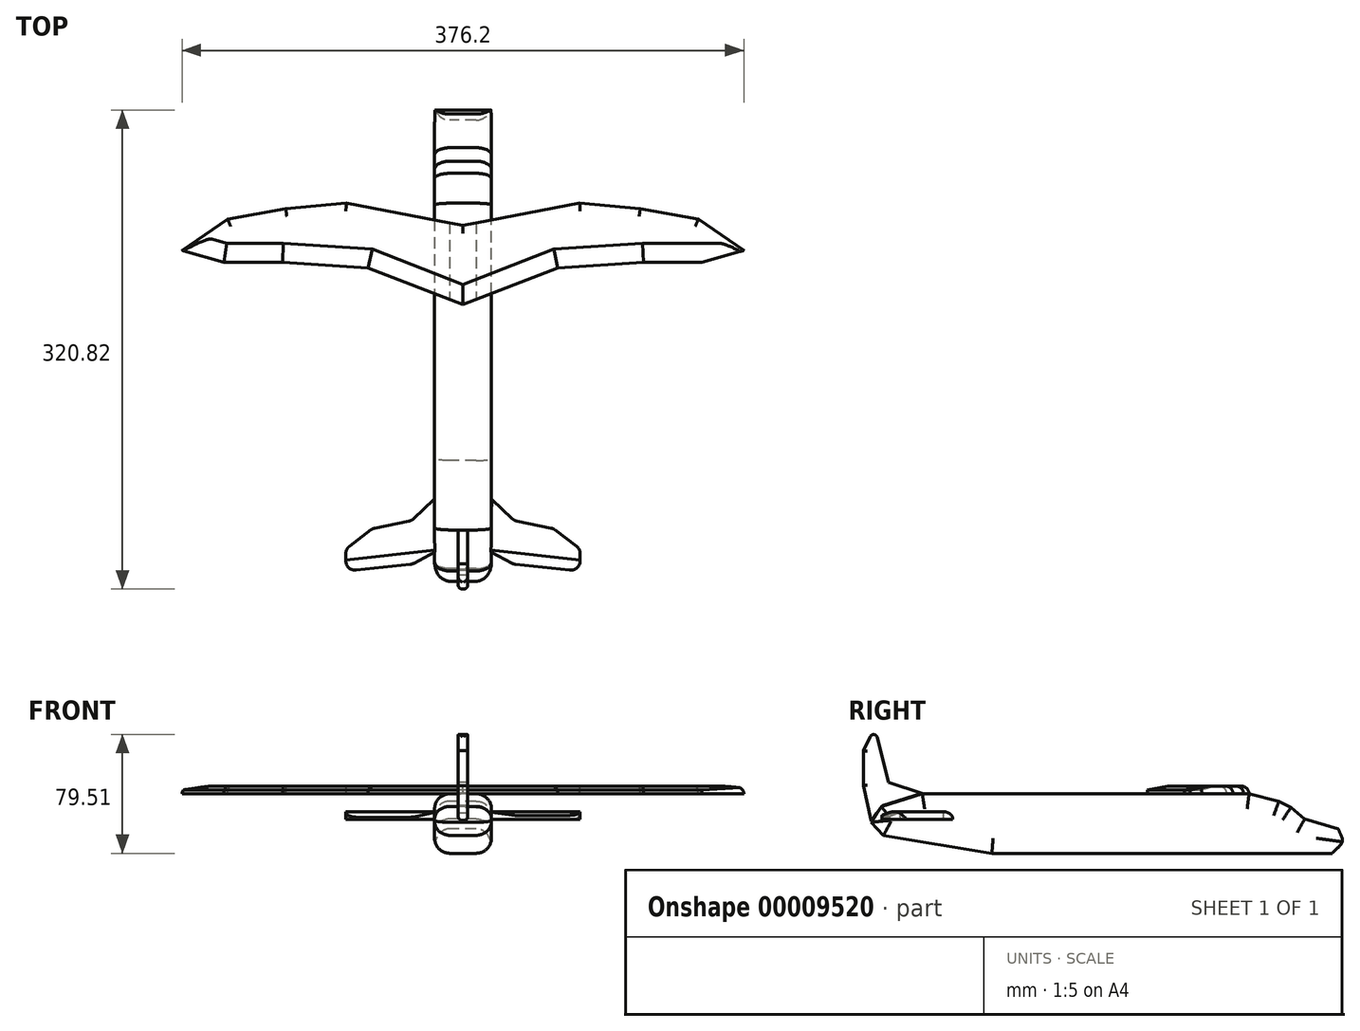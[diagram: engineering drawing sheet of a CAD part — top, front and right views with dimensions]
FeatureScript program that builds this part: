
annotation { "Feature Type Name" : "Feature", "Feature Type Description" : "" }
export const myFeature = defineFeature(function(context is Context, id is Id, definition is map)
    precondition{}
    {
        {
            var Q0;
            Q0=qCreatedBy(makeId("Right.planeOp"),FACE);
            var sketch = newSketch(context, id + "F0", { "sketchPlane" : qUnion([Q0])});
            skLineSegment(sketch, "E0", {"start": v(-78.46, 0) * mm, "end": v(149.41, 0) * mm});
            skLineSegment(sketch, "E1", {"start": v(149.41, 0) * mm, "end": v(157.23, 7.66) * mm});
            skLineSegment(sketch, "E2", {"start": v(157.23, 7.66) * mm, "end": v(153.48, 16.41) * mm});
            skLineSegment(sketch, "E3", {"start": v(153.48, 16.41) * mm, "end": v(130.97, 22.97) * mm});
            skLineSegment(sketch, "E4", {"start": v(130.97, 22.97) * mm, "end": v(121.9, 30.79) * mm});
            skLineSegment(sketch, "E5", {"start": v(121.9, 30.79) * mm, "end": v(113.78, 34.85) * mm});
            skLineSegment(sketch, "E6", {"start": v(113.78, 34.85) * mm, "end": v(93.77, 39.85) * mm});
            skLineSegment(sketch, "E7", {"start": v(93.77, 39.85) * mm, "end": v(-34.7, 39.85) * mm});
            skLineSegment(sketch, "E8", {"start": v(-34.7, 39.85) * mm, "end": v(-125.03, 39.85) * mm});
            skLineSegment(sketch, "E9", {"start": v(-125.03, 39.85) * mm, "end": v(-152.54, 31.41) * mm});
            skLineSegment(sketch, "E10", {"start": v(-152.54, 31.41) * mm, "end": v(-159.42, 20.79) * mm});
            skLineSegment(sketch, "E11", {"start": v(-159.42, 20.79) * mm, "end": v(-150.98, 12.03) * mm});
            skLineSegment(sketch, "E12", {"start": v(-150.98, 12.03) * mm, "end": v(-78.46, 0) * mm});
            skSolve(sketch);
        }
        {
            var Q0;
            Q0 = qSketchRegion(id + "F0", true);
            extrude(context, id + "F1", {"entities" : qUnion([Q0]), "endBound" : BoundingType.SYMMETRIC, "depth" : 38.1 * mm});
        }
        {
            var Q0;
            Q0=makeQuery(id+"F1.opExtrude","CAP_FACE",FACE,{"disambiguationData":[OSD([sQuery(id+"F0.wireOp",EDGE,"E0"),sQuery(id+"F0.wireOp",EDGE,"E1"),sQuery(id+"F0.wireOp",EDGE,"E2"),sQuery(id+"F0.wireOp",EDGE,"E3"),sQuery(id+"F0.wireOp",EDGE,"E4"),sQuery(id+"F0.wireOp",EDGE,"E5"),sQuery(id+"F0.wireOp",EDGE,"E6"),sQuery(id+"F0.wireOp",EDGE,"E7"),sQuery(id+"F0.wireOp",EDGE,"E8"),sQuery(id+"F0.wireOp",EDGE,"E9"),sQuery(id+"F0.wireOp",EDGE,"E10"),sQuery(id+"F0.wireOp",EDGE,"E11"),sQuery(id+"F0.wireOp",EDGE,"E12")])],"isStart":false});
            var Q1;
            Q1=makeQuery(id+"F1.opExtrude","CAP_FACE",FACE,{"disambiguationData":[OSD([sQuery(id+"F0.wireOp",EDGE,"E0"),sQuery(id+"F0.wireOp",EDGE,"E1"),sQuery(id+"F0.wireOp",EDGE,"E2"),sQuery(id+"F0.wireOp",EDGE,"E3"),sQuery(id+"F0.wireOp",EDGE,"E4"),sQuery(id+"F0.wireOp",EDGE,"E5"),sQuery(id+"F0.wireOp",EDGE,"E6"),sQuery(id+"F0.wireOp",EDGE,"E7"),sQuery(id+"F0.wireOp",EDGE,"E8"),sQuery(id+"F0.wireOp",EDGE,"E9"),sQuery(id+"F0.wireOp",EDGE,"E10"),sQuery(id+"F0.wireOp",EDGE,"E11"),sQuery(id+"F0.wireOp",EDGE,"E12")])],"isStart":true});
            fillet(context, id + "F2", {"entities" : qUnion([Q0, Q1]), "radius" : 10.16 * mm, "tangentPropagation" : true, "allowEdgeOverflow" : false});
        }
        {
            var Q0;
            Q0=makeQuery(id+"F1.opExtrude","SWEPT_EDGE",EDGE,{"disambiguationData":[OSD([sQuery(id+"F0.wireOp",EDGE,"E1"),sQuery(id+"F0.wireOp",EDGE,"E2")])]});
            fillet(context, id + "F3", {"entities" : qUnion([Q0]), "radius" : 5.08 * mm, "tangentPropagation" : true, "allowEdgeOverflow" : false});
        }
        {
            var Q0;
            Q0=makeQuery(id+"F1.opExtrude","SWEPT_FACE",FACE,{"disambiguationData":[OSD([sQuery(id+"F0.wireOp",EDGE,"E7"),sQuery(id+"F0.wireOp",EDGE,"E8")])]});
            var sketch = newSketch(context, id + "F4", { "sketchPlane" : qUnion([Q0])});
            skLineSegment(sketch, "E13", {"start": v(0, 78.89) * mm, "end": v(-78.16, 93.77) * mm});
            skLineSegment(sketch, "E14", {"start": v(-78.16, 93.77) * mm, "end": v(-118.71, 90.18) * mm});
            skLineSegment(sketch, "E15", {"start": v(-118.71, 90.18) * mm, "end": v(-157.58, 83.07) * mm});
            skLineSegment(sketch, "E16", {"start": v(-157.58, 83.07) * mm, "end": v(-188.1, 62.17) * mm});
            skLineSegment(sketch, "E17", {"start": v(-188.1, 62.17) * mm, "end": v(-160.1, 54.23) * mm});
            skLineSegment(sketch, "E18", {"start": v(-160.1, 54.23) * mm, "end": v(-120.8, 54.23) * mm});
            skLineSegment(sketch, "E19", {"start": v(-120.8, 54.23) * mm, "end": v(-63.54, 50.47) * mm});
            skLineSegment(sketch, "E20", {"start": v(-63.54, 50.47) * mm, "end": v(0, 25.8) * mm});
            skLineSegment(sketch, "E21", {"start": v(0, 0) * mm, "end": v(0, 154.96) * mm, "construction": true});
            skLineSegment(sketch, "E22.0.MirrorCS", {"start": v(78.16, 93.77) * mm, "end": v(118.71, 90.18) * mm});
            skLineSegment(sketch, "E22.1.MirrorCS", {"start": v(118.71, 90.18) * mm, "end": v(157.58, 83.07) * mm});
            skLineSegment(sketch, "E22.2.MirrorCS", {"start": v(63.54, 50.47) * mm, "end": v(0, 25.8) * mm});
            skLineSegment(sketch, "E22.3.MirrorCS", {"start": v(157.58, 83.07) * mm, "end": v(188.1, 62.17) * mm});
            skLineSegment(sketch, "E22.4.MirrorCS", {"start": v(188.1, 62.17) * mm, "end": v(160.1, 54.23) * mm});
            skLineSegment(sketch, "E22.5.MirrorCS", {"start": v(160.1, 54.23) * mm, "end": v(120.8, 54.23) * mm});
            skLineSegment(sketch, "E22.6.MirrorCS", {"start": v(0, 78.89) * mm, "end": v(78.16, 93.77) * mm});
            skLineSegment(sketch, "E22.7.MirrorCS", {"start": v(120.8, 54.23) * mm, "end": v(63.54, 50.47) * mm});
            skSolve(sketch);
        }
        {
            var Q0;
            Q0 = qSketchRegion(id + "F4", true);
            extrude(context, id + "F5", {"entities" : qUnion([Q0]), "operationType" : NewBodyOperationType.ADD, "depth" : 5.08 * mm});
        }
        {
            var Q0;
            Q0=qCreatedBy(makeId("Right.planeOp"),FACE);
            var sketch = newSketch(context, id + "F6", { "sketchPlane" : qUnion([Q0])});
            skLineSegment(sketch, "E23", {"start": v(-159.33, 21.94) * mm, "end": v(-164.55, 45.27) * mm});
            skLineSegment(sketch, "E24", {"start": v(-164.55, 45.27) * mm, "end": v(-164.55, 68.9) * mm});
            skLineSegment(sketch, "E25", {"start": v(-164.55, 68.9) * mm, "end": v(-156.87, 84.25) * mm});
            skLineSegment(sketch, "E26", {"start": v(-156.87, 84.25) * mm, "end": v(-147.67, 47.42) * mm});
            skLineSegment(sketch, "E27", {"start": v(-147.67, 47.42) * mm, "end": v(-125.26, 40.05) * mm});
            skLineSegment(sketch, "E28", {"start": v(-125.26, 40.05) * mm, "end": v(-151.66, 31.77) * mm});
            skLineSegment(sketch, "E29", {"start": v(-151.66, 31.77) * mm, "end": v(-159.33, 21.94) * mm});
            skSolve(sketch);
        }
        {
            var Q0;
            Q0=makeQuery(id+"F6.imprint","IMPRINT",FACE,{"disambiguationData":[TD([[makeQuery(id+"F6.imprint","IMPRINT",EDGE,{"derivedFrom":sQuery(id+"F6.wireOp",EDGE,"E23")}),-1.0]])]});
            extrude(context, id + "F7", {"entities" : qUnion([Q0]), "operationType" : NewBodyOperationType.ADD, "endBound" : BoundingType.SYMMETRIC, "depth" : 6.35 * mm});
        }
        {
            var Q0;
            Q0=makeQuery(id+"F7.opExtrude","CAP_EDGE",EDGE,{"disambiguationData":[OSD([sQuery(id+"F6.wireOp",EDGE,"E25")])],"isStart":false});
            var Q1;
            Q1=makeQuery(id+"F7.opExtrude","CAP_EDGE",EDGE,{"disambiguationData":[OSD([sQuery(id+"F6.wireOp",EDGE,"E24")])],"isStart":false});
            var Q2;
            Q2=makeQuery(id+"F7.opExtrude","CAP_EDGE",EDGE,{"disambiguationData":[OSD([sQuery(id+"F6.wireOp",EDGE,"E23")])],"isStart":false});
            var Q3;
            Q3=makeQuery(id+"F7.opExtrude","CAP_EDGE",EDGE,{"disambiguationData":[OSD([sQuery(id+"F6.wireOp",EDGE,"E23")])],"isStart":true});
            var Q4;
            Q4=makeQuery(id+"F7.opExtrude","CAP_EDGE",EDGE,{"disambiguationData":[OSD([sQuery(id+"F6.wireOp",EDGE,"E24")])],"isStart":true});
            var Q5;
            Q5=makeQuery(id+"F7.opExtrude","CAP_EDGE",EDGE,{"disambiguationData":[OSD([sQuery(id+"F6.wireOp",EDGE,"E25")])],"isStart":true});
            var Q6;
            Q6=makeQuery(id+"F7.opExtrude","SWEPT_EDGE",EDGE,{"disambiguationData":[OSD([sQuery(id+"F6.wireOp",EDGE,"E25"),sQuery(id+"F6.wireOp",EDGE,"E26")])]});
            fillet(context, id + "F8", {"entities" : qUnion([Q0, Q1, Q2, Q3, Q4, Q5, Q6]), "radius" : 2.54 * mm, "tangentPropagation" : true, "allowEdgeOverflow" : false});
        }
        {
            var Q0;
            Q0=qCreatedBy(makeId("Top.planeOp"),FACE);
            cPlane(context, id + "F9", {"entities" : qUnion([Q0]), "cplaneType" : CPlaneType.OFFSET, "offset" : 25.4 * mm, "width" : 152.4 * mm, "height" : 152.4 * mm});
        }
        {
            var Q0;
            Q0=qCreatedBy(id+"F9.planeOp",FACE);
            var sketch = newSketch(context, id + "F10", { "sketchPlane" : qUnion([Q0])});
            skLineSegment(sketch, "E30", {"start": v(19.38, -104.66) * mm, "end": v(33.06, -117.54) * mm});
            skLineSegment(sketch, "E31", {"start": v(36.15, -119.14) * mm, "end": v(58.99, -123.79) * mm});
            skLineSegment(sketch, "E32", {"start": v(61.55, -124.94) * mm, "end": v(75.97, -135.84) * mm});
            skLineSegment(sketch, "E33", {"start": v(78.49, -140.9) * mm, "end": v(78.49, -145.67) * mm});
            skLineSegment(sketch, "E34", {"start": v(71.45, -151.98) * mm, "end": v(35.17, -148.03) * mm});
            skLineSegment(sketch, "E35", {"start": v(32.84, -147.3) * mm, "end": v(17.61, -139.07) * mm});
            skLineSegment(sketch, "E36", {"start": v(19.38, -104.66) * mm, "end": v(17.61, -139.07) * mm});
            skPoint(sketch, "E37.visualSharp", {"position": v(78.49, -137.75) * mm});
            skArc(sketch, "E37.filletArc", {"start": v(78.49, -140.9) * mm, "mid": v(77.82, -138.08) * mm, "end": v(75.97, -135.84) * mm});
            skPoint(sketch, "E38.visualSharp", {"position": v(78.49, -152.74) * mm});
            skArc(sketch, "E38.filletArc", {"start": v(71.45, -151.98) * mm, "mid": v(76.38, -150.4) * mm, "end": v(78.49, -145.67) * mm});
            skPoint(sketch, "E39.visualSharp", {"position": v(60.4, -124.07) * mm});
            skArc(sketch, "E39.filletArc", {"start": v(61.55, -124.94) * mm, "mid": v(60.33, -124.22) * mm, "end": v(58.99, -123.79) * mm});
            skPoint(sketch, "E40.visualSharp", {"position": v(34.38, -118.78) * mm});
            skArc(sketch, "E40.filletArc", {"start": v(33.06, -117.54) * mm, "mid": v(34.5, -118.56) * mm, "end": v(36.15, -119.14) * mm});
            skPoint(sketch, "E41.visualSharp", {"position": v(33.93, -147.9) * mm});
            skArc(sketch, "E41.filletArc", {"start": v(32.84, -147.3) * mm, "mid": v(33.97, -147.78) * mm, "end": v(35.17, -148.03) * mm});
            skLineSegment(sketch, "E42", {"start": v(0, 0) * mm, "end": v(0, -233.9) * mm, "construction": true});
            skLineSegment(sketch, "E43.0.MirrorCS", {"start": v(-71.45, -151.98) * mm, "end": v(-35.17, -148.03) * mm});
            skLineSegment(sketch, "E44.0.MirrorCS", {"start": v(-78.49, -140.9) * mm, "end": v(-78.49, -145.67) * mm});
            skArc(sketch, "E44.1.MirrorCS", {"start": v(-78.49, -140.9) * mm, "mid": v(-77.82, -138.08) * mm, "end": v(-75.97, -135.84) * mm});
            skArc(sketch, "E44.2.MirrorCS", {"start": v(-61.55, -124.94) * mm, "mid": v(-60.33, -124.22) * mm, "end": v(-58.99, -123.79) * mm});
            skArc(sketch, "E44.3.MirrorCS", {"start": v(-32.84, -147.3) * mm, "mid": v(-33.97, -147.78) * mm, "end": v(-35.17, -148.03) * mm});
            skArc(sketch, "E44.4.MirrorCS", {"start": v(-33.06, -117.54) * mm, "mid": v(-34.5, -118.56) * mm, "end": v(-36.15, -119.14) * mm});
            skArc(sketch, "E44.5.MirrorCS", {"start": v(-71.45, -151.98) * mm, "mid": v(-76.38, -150.4) * mm, "end": v(-78.49, -145.67) * mm});
            skLineSegment(sketch, "E44.7.MirrorCS", {"start": v(-19.38, -104.66) * mm, "end": v(-17.61, -139.07) * mm});
            skPoint(sketch, "E44.8.MirrorP", {"position": v(-60.4, -124.07) * mm});
            skPoint(sketch, "E44.9.MirrorP", {"position": v(-78.49, -137.75) * mm});
            skLineSegment(sketch, "E44.10.MirrorCS", {"start": v(-32.84, -147.3) * mm, "end": v(-17.61, -139.07) * mm});
            skPoint(sketch, "E44.11.MirrorP", {"position": v(-33.93, -147.9) * mm});
            skPoint(sketch, "E44.12.MirrorP", {"position": v(-78.49, -152.74) * mm});
            skLineSegment(sketch, "E44.13.MirrorCS", {"start": v(-61.55, -124.94) * mm, "end": v(-75.97, -135.84) * mm});
            skPoint(sketch, "E44.14.MirrorP", {"position": v(-34.38, -118.78) * mm});
            skLineSegment(sketch, "E44.15.MirrorCS", {"start": v(-19.38, -104.66) * mm, "end": v(-33.06, -117.54) * mm});
            skLineSegment(sketch, "E44.16.MirrorCS", {"start": v(-36.15, -119.14) * mm, "end": v(-58.99, -123.79) * mm});
            skSolve(sketch);
        }
        {
            var Q0;
            Q0=makeQuery(id+"F10.imprint","IMPRINT",FACE,{"disambiguationData":[TD([[makeQuery(id+"F10.imprint","IMPRINT",EDGE,{"derivedFrom":sQuery(id+"F10.wireOp",EDGE,"E30")}),-1.0]])]});
            var Q1;
            Q1=makeQuery(id+"F10.imprint","IMPRINT",FACE,{"disambiguationData":[TD([[makeQuery(id+"F10.imprint","IMPRINT",EDGE,{"derivedFrom":sQuery(id+"F10.wireOp",EDGE,"E44.0.MirrorCS")}),1.0]])]});
            extrude(context, id + "F11", {"entities" : qUnion([Q0, Q1]), "operationType" : NewBodyOperationType.ADD, "endBound" : BoundingType.SYMMETRIC, "depth" : 5.08 * mm});
        }
        {
            var Q0;
            Q0=makeQuery(id+"F5.opExtrude","CAP_EDGE",EDGE,{"disambiguationData":[OSD([sQuery(id+"F4.wireOp",EDGE,"E13")])],"isStart":false});
            var Q1;
            Q1=makeQuery(id+"F5.opExtrude","CAP_EDGE",EDGE,{"disambiguationData":[OSD([sQuery(id+"F4.wireOp",EDGE,"E22.6.MirrorCS")])],"isStart":false});
            var Q2;
            Q2=makeQuery(id+"F5.opExtrude","CAP_EDGE",EDGE,{"disambiguationData":[OSD([sQuery(id+"F4.wireOp",EDGE,"E22.1.MirrorCS")])],"isStart":false});
            var Q3;
            Q3=makeQuery(id+"F5.opExtrude","CAP_EDGE",EDGE,{"disambiguationData":[OSD([sQuery(id+"F4.wireOp",EDGE,"E22.0.MirrorCS")])],"isStart":false});
            var Q4;
            Q4=makeQuery(id+"F5.opExtrude","CAP_EDGE",EDGE,{"disambiguationData":[OSD([sQuery(id+"F4.wireOp",EDGE,"E14")])],"isStart":false});
            var Q5;
            Q5=makeQuery(id+"F5.opExtrude","CAP_EDGE",EDGE,{"disambiguationData":[OSD([sQuery(id+"F4.wireOp",EDGE,"E15")])],"isStart":false});
            var Q6;
            Q6=makeQuery(id+"F5.opExtrude","CAP_EDGE",EDGE,{"disambiguationData":[OSD([sQuery(id+"F4.wireOp",EDGE,"E16")])],"isStart":false});
            var Q7;
            Q7=makeQuery(id+"F5.opExtrude","CAP_EDGE",EDGE,{"disambiguationData":[OSD([sQuery(id+"F4.wireOp",EDGE,"E22.3.MirrorCS")])],"isStart":false});
            var Q8;
            Q8=makeQuery(id+"F11.opExtrude","CAP_EDGE",EDGE,{"disambiguationData":[OSD([sQuery(id+"F10.wireOp",EDGE,"E30")])],"isStart":false});
            var Q9;
            Q9=makeQuery(id+"F11.opExtrude","CAP_EDGE",EDGE,{"disambiguationData":[OSD([sQuery(id+"F10.wireOp",EDGE,"E44.15.MirrorCS")])],"isStart":false});
            var Q10;
            Q10=makeQuery(id+"F11.opExtrude","CAP_EDGE",EDGE,{"disambiguationData":[OSD([sQuery(id+"F10.wireOp",EDGE,"E40.filletArc")])],"isStart":false});
            var Q11;
            Q11=makeQuery(id+"F11.opExtrude","CAP_EDGE",EDGE,{"disambiguationData":[OSD([sQuery(id+"F10.wireOp",EDGE,"E31")])],"isStart":false});
            var Q12;
            Q12=makeQuery(id+"F11.opExtrude","CAP_EDGE",EDGE,{"disambiguationData":[OSD([sQuery(id+"F10.wireOp",EDGE,"E39.filletArc")])],"isStart":false});
            var Q13;
            Q13=makeQuery(id+"F11.opExtrude","CAP_EDGE",EDGE,{"disambiguationData":[OSD([sQuery(id+"F10.wireOp",EDGE,"E32")])],"isStart":false});
            var Q14;
            Q14=makeQuery(id+"F11.opExtrude","CAP_EDGE",EDGE,{"disambiguationData":[OSD([sQuery(id+"F10.wireOp",EDGE,"E37.filletArc")])],"isStart":false});
            var Q15;
            Q15=makeQuery(id+"F11.opExtrude","CAP_EDGE",EDGE,{"disambiguationData":[OSD([sQuery(id+"F10.wireOp",EDGE,"E44.4.MirrorCS")])],"isStart":false});
            var Q16;
            Q16=makeQuery(id+"F11.opExtrude","CAP_EDGE",EDGE,{"disambiguationData":[OSD([sQuery(id+"F10.wireOp",EDGE,"E44.16.MirrorCS")])],"isStart":false});
            var Q17;
            Q17=makeQuery(id+"F11.opExtrude","SWEPT_EDGE",EDGE,{"disambiguationData":[OSD([sQuery(id+"F10.wireOp",EDGE,"E44.2.MirrorCS"),sQuery(id+"F10.wireOp",EDGE,"E44.13.MirrorCS")])]});
            var Q18;
            Q18=makeQuery(id+"F11.opExtrude","CAP_EDGE",EDGE,{"disambiguationData":[OSD([sQuery(id+"F10.wireOp",EDGE,"E44.13.MirrorCS")])],"isStart":false});
            fillet(context, id + "F12", {"entities" : qUnion([Q0, Q1, Q2, Q3, Q4, Q5, Q6, Q7, Q8, Q9, Q10, Q11, Q12, Q13, Q14, Q15, Q16, Q17, Q18]), "radius" : 5.08 * mm, "allowEdgeOverflow" : false});
        }
        {
            var Q0;
            Q0=makeQuery(id+"F5.opExtrude","CAP_EDGE",EDGE,{"disambiguationData":[OSD([sQuery(id+"F4.wireOp",EDGE,"E22.5.MirrorCS")])],"isStart":false});
            var Q1;
            Q1=makeQuery(id+"F5.opExtrude","CAP_EDGE",EDGE,{"disambiguationData":[OSD([sQuery(id+"F4.wireOp",EDGE,"E22.7.MirrorCS")])],"isStart":false});
            var Q2;
            Q2=makeQuery(id+"F5.opExtrude","CAP_EDGE",EDGE,{"disambiguationData":[OSD([sQuery(id+"F4.wireOp",EDGE,"E22.2.MirrorCS")])],"isStart":false});
            var Q3;
            Q3=makeQuery(id+"F5.opExtrude","CAP_EDGE",EDGE,{"disambiguationData":[OSD([sQuery(id+"F4.wireOp",EDGE,"E20")])],"isStart":false});
            var Q4;
            Q4=makeQuery(id+"F5.opExtrude","CAP_EDGE",EDGE,{"disambiguationData":[OSD([sQuery(id+"F4.wireOp",EDGE,"E19")])],"isStart":false});
            var Q5;
            Q5=makeQuery(id+"F5.opExtrude","CAP_EDGE",EDGE,{"disambiguationData":[OSD([sQuery(id+"F4.wireOp",EDGE,"E18")])],"isStart":false});
            var Q6;
            Q6=makeQuery(id+"F5.opExtrude","CAP_EDGE",EDGE,{"disambiguationData":[OSD([sQuery(id+"F4.wireOp",EDGE,"E17")])],"isStart":false});
            chamfer(context, id + "F13", {"entities" : qUnion([Q0, Q1, Q2, Q3, Q4, Q5, Q6]), "chamferType" : ChamferType.TWO_OFFSETS, "width1" : 2.54 * mm, "oppositeDirection" : false, "width2" : 12.7 * mm});
        }
        {
            var Q0;
            Q0=makeQuery(id+"F11.opExtrude","CAP_EDGE",EDGE,{"disambiguationData":[OSD([sQuery(id+"F10.wireOp",EDGE,"E43.0.MirrorCS")])],"isStart":false});
            chamfer(context, id + "F14", {"entities" : qUnion([Q0]), "chamferType" : ChamferType.TWO_OFFSETS, "width1" : 7.62 * mm, "oppositeDirection" : false, "width2" : 3.8 * mm});
        }
        {
            var Q0;
            Q0=makeQuery(id+"F11.opExtrude","CAP_EDGE",EDGE,{"disambiguationData":[OSD([sQuery(id+"F10.wireOp",EDGE,"E34")])],"isStart":false});
            chamfer(context, id + "F15", {"entities" : qUnion([Q0]), "chamferType" : ChamferType.TWO_OFFSETS, "width1" : 2.54 * mm, "oppositeDirection" : false, "width2" : 7.62 * mm});
        }
    });
